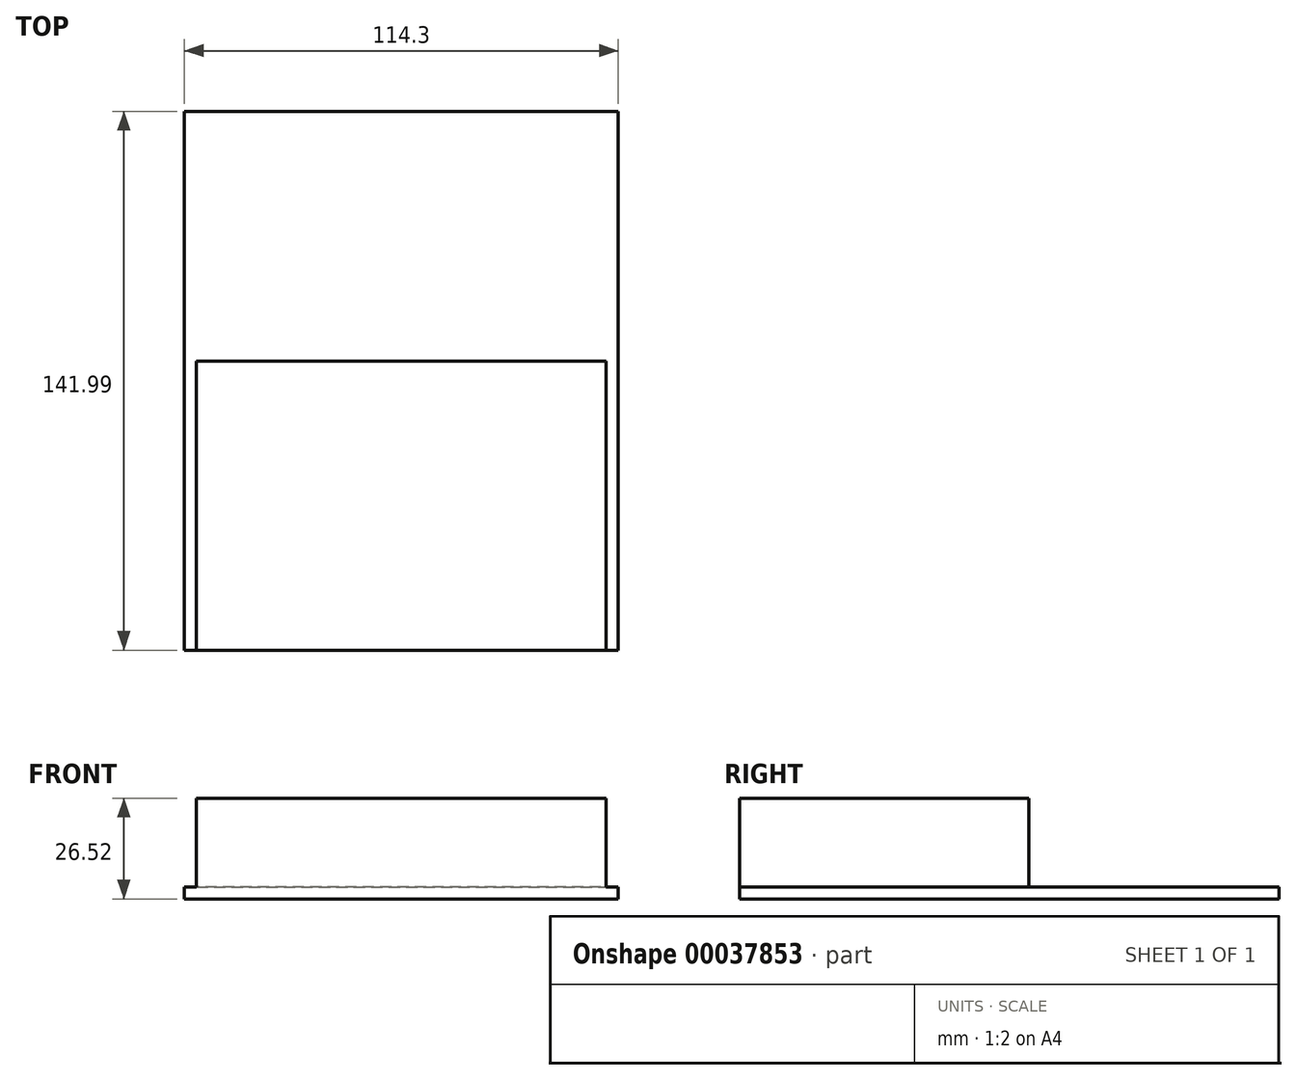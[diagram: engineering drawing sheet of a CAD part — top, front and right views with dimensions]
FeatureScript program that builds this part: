
annotation { "Feature Type Name" : "Feature", "Feature Type Description" : "" }
export const myFeature = defineFeature(function(context is Context, id is Id, definition is map)
    precondition{}
    {
        {
            var Q0;
            Q0=qCreatedBy(makeId("Top.planeOp"),FACE);
            var sketch = newSketch(context, id + "F0", { "sketchPlane" : qUnion([Q0])});
            skLineSegment(sketch, "E0.rect.bottom", {"start": v(-53.97, 38.1) * mm, "end": v(53.98, 38.1) * mm});
            skLineSegment(sketch, "E0.rect.top", {"start": v(-53.97, -38.1) * mm, "end": v(53.97, -38.1) * mm});
            skLineSegment(sketch, "E0.rect.left", {"start": v(-53.97, 38.1) * mm, "end": v(-53.98, -38.1) * mm});
            skLineSegment(sketch, "E0.rect.right", {"start": v(53.98, 38.1) * mm, "end": v(53.97, -38.1) * mm});
            skPoint(sketch, "E0.rect.middle", {"position": v(0, 0) * mm});
            skSolve(sketch);
        }
        {
            var Q0;
            Q0=makeQuery(id+"F0.imprint","IMPRINT",FACE,{"disambiguationData":[TD([[makeQuery(id+"F0.imprint","IMPRINT",EDGE,{"derivedFrom":sQuery(id+"F0.wireOp",EDGE,"E0.rect.bottom")}),-1.0]])]});
            extrude(context, id + "F1", {"entities" : qUnion([Q0]), "depth" : 23.35 * mm});
        }
        {
            var Q0;
            Q0=makeQuery(id+"F1.opExtrude","CAP_FACE",FACE,{"disambiguationData":[OSD([sQuery(id+"F0.wireOp",EDGE,"E0.rect.bottom"),sQuery(id+"F0.wireOp",EDGE,"E0.rect.top"),sQuery(id+"F0.wireOp",EDGE,"E0.rect.left"),sQuery(id+"F0.wireOp",EDGE,"E0.rect.right")])],"isStart":true});
            var sketch = newSketch(context, id + "F2", { "sketchPlane" : qUnion([Q0])});
            skLineSegment(sketch, "E1.bottom", {"start": v(57.15, 38.1) * mm, "end": v(-57.15, 38.1) * mm});
            skLineSegment(sketch, "E1.top", {"start": v(57.15, -103.9) * mm, "end": v(-57.15, -103.9) * mm});
            skLineSegment(sketch, "E1.left", {"start": v(57.15, 38.1) * mm, "end": v(57.15, -103.9) * mm});
            skLineSegment(sketch, "E1.right", {"start": v(-57.15, 38.1) * mm, "end": v(-57.15, -103.9) * mm});
            skLineSegment(sketch, "E2", {"start": v(0, -103.9) * mm, "end": v(0, -38.1) * mm, "construction": true});
            skSolve(sketch);
        }
        {
            var Q0;
            Q0 = qSketchRegion(id + "F2", true);
            extrude(context, id + "F3", {"entities" : qUnion([Q0]), "operationType" : NewBodyOperationType.ADD, "depth" : 3.17 * mm});
        }
    });
